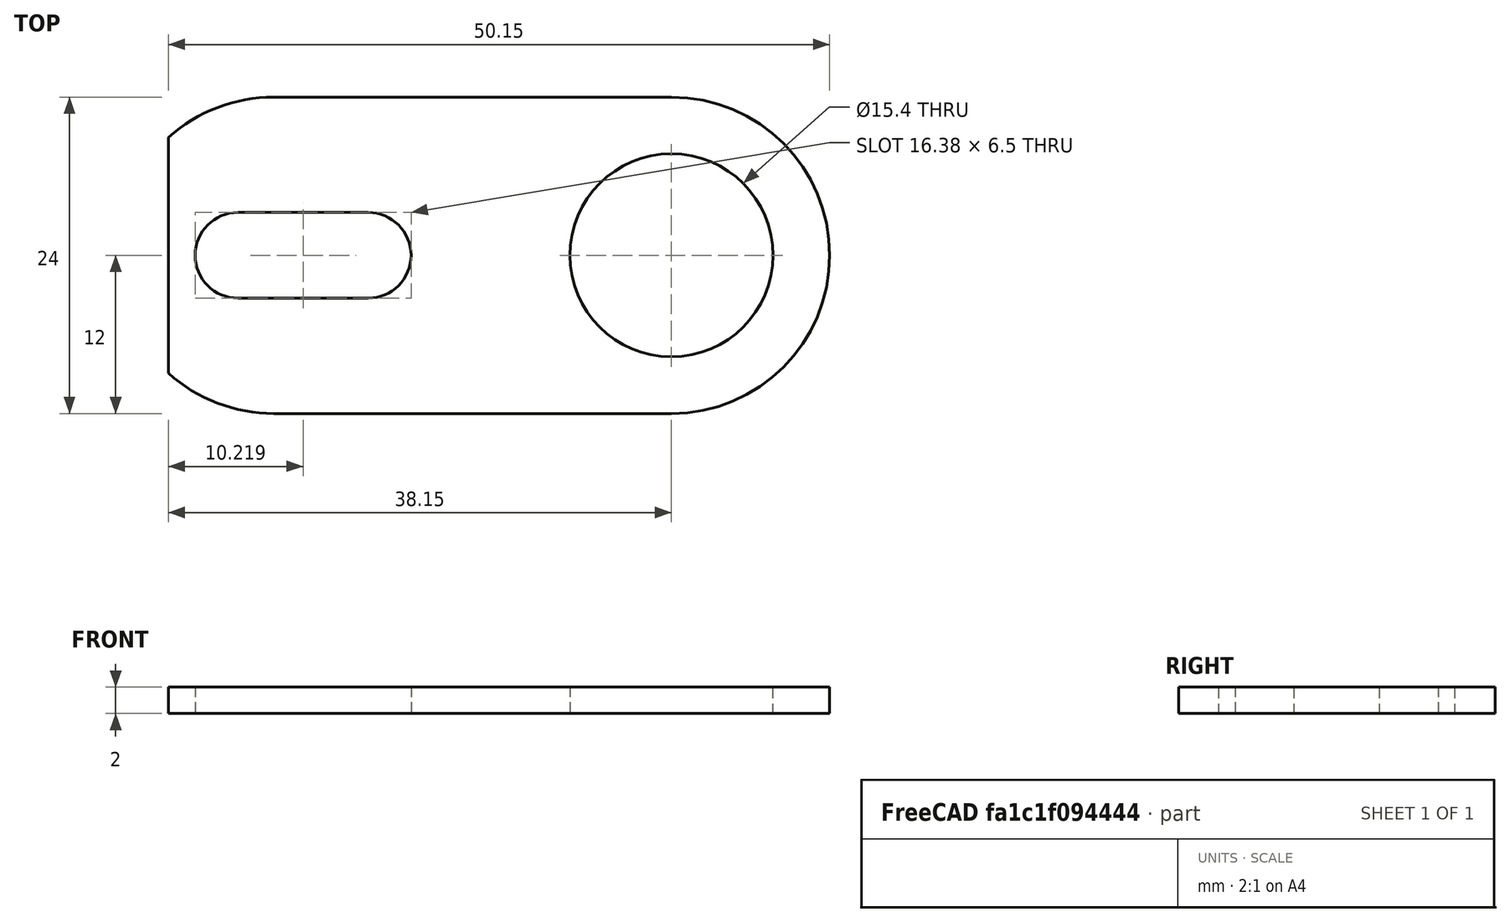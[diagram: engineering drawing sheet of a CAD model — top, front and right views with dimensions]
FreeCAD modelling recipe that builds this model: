
FCSTD DOCUMENT  (FreeCAD 0.16R)
Label: spacer
License: All rights reserved
LicenseURL: http://en.wikipedia.org/wiki/All_rights_reserved
objects: Mesh::Feature×2, Sketcher::SketchObject×1, PartDesign::Pad×1
note: 3 computed .brp shape members not serialized (recipe doc carries the construction recipe); baked Part::Feature solids carry a one-line shape summary decoded from their .brp

FEATURE [Sketcher::SketchObject] Sketch
  sketch-geometry (11):
    g0: Circle CenterX=31 CenterY=0 CenterZ=0 NormalX=0 NormalY=0 NormalZ=1 Radius=7.7
    g1: ArcOfCircle CenterX=31 CenterY=0 CenterZ=0 NormalX=0 NormalY=0 NormalZ=1 Radius=12 StartAngle=4.71239 EndAngle=7.85398
    g2: ArcOfCircle CenterX=0.850795 CenterY=0 CenterZ=0 NormalX=0 NormalY=0 NormalZ=1 Radius=12 StartAngle=1.5708 EndAngle=2.30052
    g3: LineSegment StartX=31 StartY=12 StartZ=0 EndX=0.850795 EndY=12 EndZ=0
    g4: LineSegment StartX=31 StartY=-12 StartZ=0 EndX=0.850795 EndY=-12 EndZ=0
    g5: LineSegment StartX=-7.14921 StartY=8.94427 StartZ=0 EndX=-7.14921 EndY=-8.94427 EndZ=0
    g6: ArcOfCircle CenterX=0.850795 CenterY=0 CenterZ=0 NormalX=0 NormalY=0 NormalZ=1 Radius=12 StartAngle=3.98266 EndAngle=4.71239
    g7: ArcOfCircle CenterX=-1.87072 CenterY=0 CenterZ=0 NormalX=0 NormalY=0 NormalZ=1 Radius=3.25 StartAngle=1.5708 EndAngle=4.71239
    g8: ArcOfCircle CenterX=8.00927 CenterY=0 CenterZ=0 NormalX=0 NormalY=0 NormalZ=1 Radius=3.25 StartAngle=4.71239 EndAngle=7.85398
    g9: LineSegment StartX=-1.87072 StartY=-3.25 StartZ=0 EndX=8.00927 EndY=-3.25 EndZ=0
    g10: LineSegment StartX=-1.87072 StartY=3.25 StartZ=0 EndX=8.00927 EndY=3.25 EndZ=0
  constraints (25):
    c: Radius(g0) = 7.7
    c: PointOnObject(g0,g-1)
    c: Tangent(g1,g4) = 1.5708
    c: Tangent(g1,g3) = -1.5708
    c: Tangent(g3,g2) = -1.5708
    c: Tangent(g4,g6) = 1.5708
    c: Horizontal(g3)
    c: Equal(g1,g2)
    c: Coincident(g1,g0)
    c: Distance(g6,g2) = 24
    c: Vertical(g5)
    c: Equal(g2,g6)
    c: Coincident(g2,g6)
    c: Coincident(g5,g2)
    c: Coincident(g5,g6)
    c: DistanceX(g2,g2) = 8
    c: Tangent(g7,g10) = 1.5708
    c: Tangent(g7,g9) = -1.5708
    c: Tangent(g9,g8) = -1.5708
    c: Tangent(g10,g8) = 1.5708
    c: Horizontal(g9)
    c: Equal(g7,g8)
    c: DistanceY(g-1,g7) = 3.25
    c: DistanceY(g7,g-1) = 3.25
    c: DistanceX(g-1,g0) = 31
FEATURE [PartDesign::Pad] Pad
  Length = 2
  Length2 = 100
  Sketch = -> Sketch
  Type = 0
FEATURE [Mesh::Feature] Mesh  label="Pad (Meshed)"
FEATURE [Mesh::Feature] Mesh001  label="Pad (Meshed)001"
